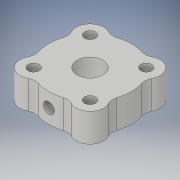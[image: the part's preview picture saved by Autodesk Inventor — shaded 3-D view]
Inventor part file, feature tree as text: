
AUTODESK INVENTOR PART (.ipt)
format: ipt  version: 2019 (Build 230136000, 136)  size: 149,504 bytes
history: native  units: mm
features: fillet x1
ambient origin geometry x8: Origin, YZ Plane, XZ Plane, XY Plane, X Axis, Y Axis, Z Axis, Center Point
bodies: Solid1 (feature_tree)
feature tree (1):
  fillet  "Fillet1"  [1 undecoded]
note: 1 required parameter value undecoded (feature->parameter linkage not recoverable at this tier; creation-order binding heuristic only, values carry confidence <= 0.55)
